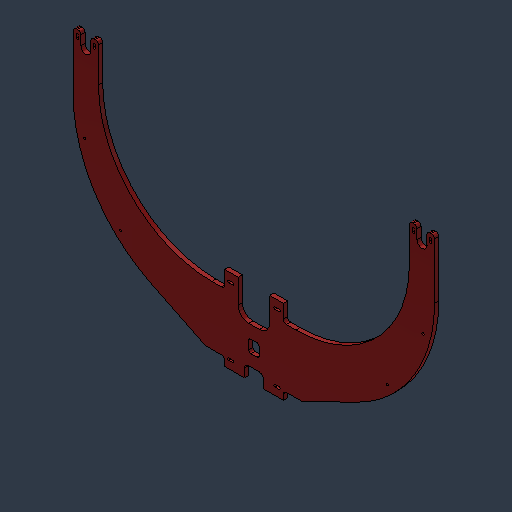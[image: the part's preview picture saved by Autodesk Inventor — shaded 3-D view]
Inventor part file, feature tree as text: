
AUTODESK INVENTOR PART (.ipt)
format: ipt  version: 2024.3 (Build 283343000, 343)  size: 161,792 bytes
history: native  units: mm (DEFAULTED — no unit token found)
features: fillet x1
ambient origin geometry x8: Origin, YZ Plane, XZ Plane, XY Plane, X Axis, Y Axis, Z Axis, Center Point
bodies: Solid1 (feature_tree)
feature tree (1):
  fillet  "Fillet5"  [1 undecoded]
note: 1 required parameter value undecoded (feature->parameter linkage not recoverable at this tier; creation-order binding heuristic only, values carry confidence <= 0.55)
